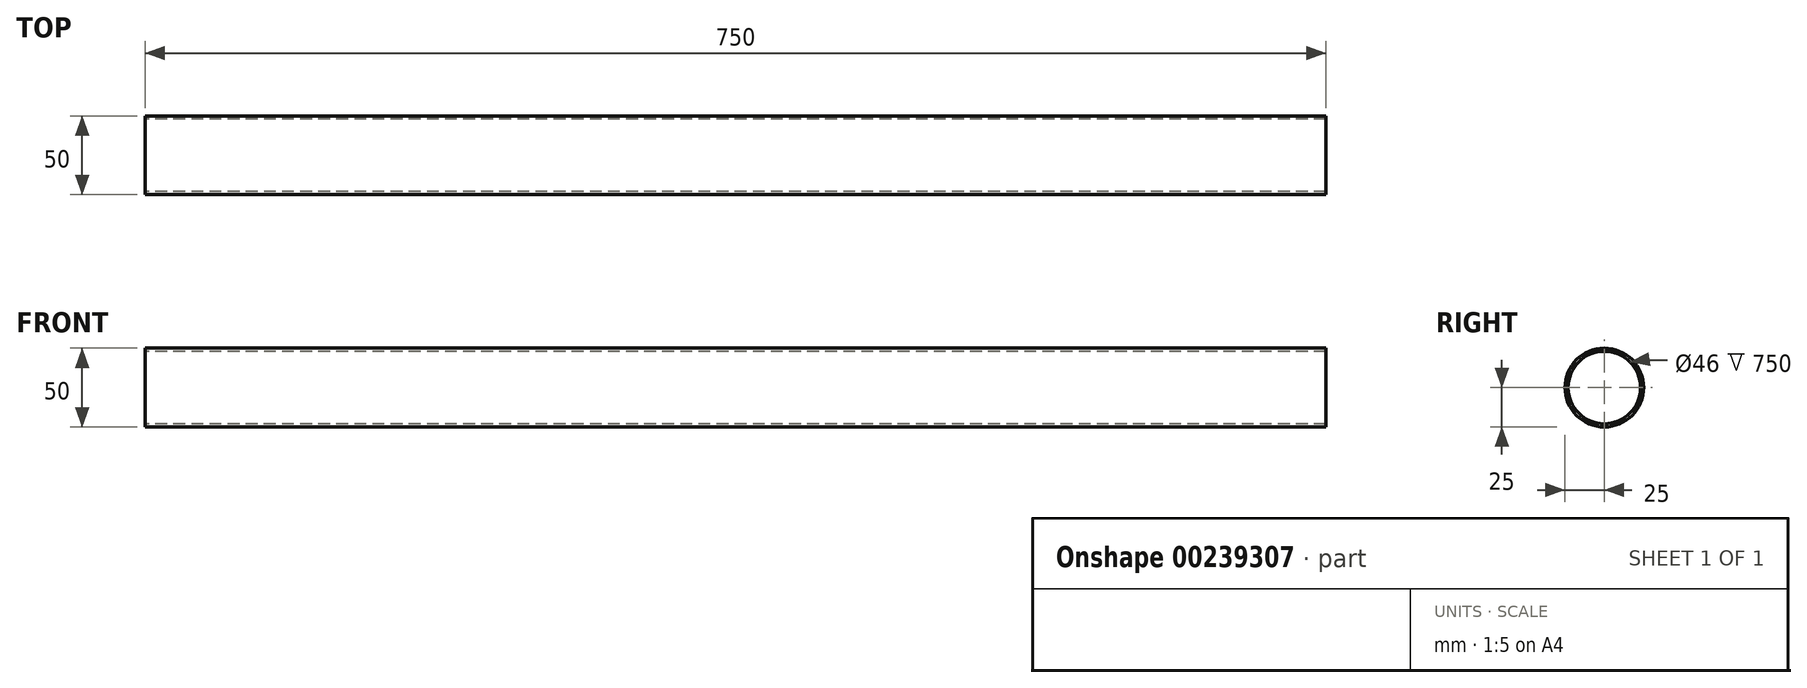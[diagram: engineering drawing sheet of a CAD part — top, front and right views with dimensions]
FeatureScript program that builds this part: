
annotation { "Feature Type Name" : "Feature", "Feature Type Description" : "" }
export const myFeature = defineFeature(function(context is Context, id is Id, definition is map)
    precondition{}
    {
        {
            var Q0;
            Q0=qCreatedBy(makeId("Right.planeOp"),FACE);
            var sketch = newSketch(context, id + "F0", { "sketchPlane" : qUnion([Q0])});
            skCircle(sketch, "E0", {"center": v(0, 0) * mm, "radius": 25 * mm});
            skCircle(sketch, "E1", {"center": v(0, 0) * mm, "radius": 23 * mm});
            skSolve(sketch);
        }
        {
            var Q0;
            Q0 = qSketchRegion(id + "F0", true);
            extrude(context, id + "F1", {"entities" : qUnion([Q0]), "depth" : 750 * mm});
        }
    });
